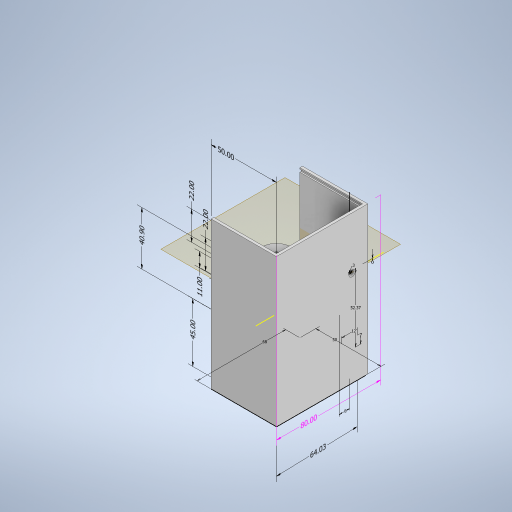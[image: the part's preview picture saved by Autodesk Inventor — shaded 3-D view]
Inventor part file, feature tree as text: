
AUTODESK INVENTOR PART (.ipt)
format: ipt  version: 2023 (Build 270158000, 158)  size: 996,352 bytes
history: native  units: in
note: dims shown in document units (in); Inventor stores cm internally (conversion verified against a paired STEP export)
features: extrude x23, sketch x22, other x10, fillet x2, plane x1
ambient origin geometry x8: Origin, YZ Plane, XZ Plane, XY Plane, X Axis, Y Axis, Z Axis, Center Point
bodies: Solid1 (feature_tree)
feature tree (58):
  other  "Annotations"
  sketch  "Sketch1"  dims[d0=2.6772in d1=1.9685in]
  extrude  "left wall"  Depth=1.9685in
  extrude  "bottom wall"  Depth=0.0787in
  extrude  "mid wall"  Depth=0.1181in
  extrude  "middle bearing hole"  Depth=1.8898in TaperAngle=0.0deg
  extrude  "back wall"  Depth=1.8898in TaperAngle=0.0deg
  extrude  "thicker mid wall ring for bearing"  Depth=4.3661in TaperAngle=0.0deg
  extrude  "motor attachment wall"  Depth=0.0197in TaperAngle=0.0deg
  extrude  "motor holes"  Depth=0.1142in
  extrude  "motor attachment wall cut out"  Depth=0.2323in
  extrude  "mid wall cut out"  Depth=1.8898in TaperAngle=0.0deg
  extrude  "encoder wall"  Depth=1.8898in
  extrude  "encoder holes"  Depth=0.9449in
  extrude  "encoder wall cut out"  Depth=0.1772in
  extrude  "top"  Depth=0.7087in
  sketch  "Sketch31"  dims[d136=0.9449in d137=0.9449in]
  extrude  "top rightWallGroove"  Depth=0.9449in
  extrude  "back rightWallGroove"  Depth=0.9449in
  extrude  "bottom rightWallGroove"  Depth=0.315in TaperAngle=0.0deg
  extrude  "encoder bearing thicker"  Depth=0.0787in
  plane  "Work Plane4"
  sketch  "Sketch38"  dims[d146=1.8898in d147=0.0in]
  extrude  "loadcell block"  TaperAngle=0.0deg  [1 undecoded]
  extrude  "wire exit"  Depth=0.2362in
  extrude  "loadcell screw holes"  Depth=0.1102in
  extrude  "Extrusion32"  Depth=1.8898in
  fillet  "Fillet1"  [1 undecoded]
  fillet  "Fillet2"  Radius=0.8661in
  extrude  "load cell block support"  Depth=1.8898in
  sketch  "Sketch3"  dims[d2=0.0787in d3=0.0in d4=0.0787in]
  sketch  "Sketch10"  dims[d5=4.3661in d6=0.0in d33=0.1181in]
  sketch  "Sketch11"  dims[d34=2.3189in d35=1.8898in d36=0.0in]
  sketch  "Sketch15"  dims[d37=0.2283in d38=1.8898in d39=0.0in]
  sketch  "Sketch20"  dims[d69=0.0787in d70=4.3661in d71=0.0in]
  sketch  "Sketch21"  dims[d106=0.315in d107=0.0197in d108=0.0in]
  sketch  "Sketch24"  dims[d110=1.7717in d111=0.1142in]
  sketch  "Sketch25"  dims[d112=3.1496in d113=0.0in d119=0.2323in]
  sketch  "Sketch27"  dims[d125=1.8898in d126=2.4606in]
  sketch  "Sketch29"  dims[d131=0.063in d132=0.1772in]
  sketch  "Sketch30"  dims[d133=0.1772in d134=0.7087in]
  sketch  "Sketch32"  dims[d138=0.9449in d139=0.9449in]
  sketch  "Sketch34"  dims[d140=0.315in d141=0.1772in d142=0.1211in d143=0.0in]
  sketch  "Sketch35"  dims[d144=3.3031in d145=0.0787in]
  sketch  "Sketch39"  dims[d153=0.2362in d154=0.3346in]
  sketch  "Sketch40"  dims[d155=0.3346in d156=0.1102in]
  sketch  "Sketch41"  dims[d157=0.1102in d158=1.8898in d159=0.0in d160=0.8661in d161=1.8898in d162=0.0in d163=0.0787in d164=0.0in d165=0.0394in d166=0.0787in d167=0.0394in d168=0.0in d169=0.0787in d170=0.0394in d171=0.0in d172=0.0394in d173=0.0787in d174=0.0394in d175=0.0394in d176=0.0in d177=0.0394in d178=0.0394in d179=0.0787in d180=0.0394in d181=0.0in d182=0.3543in d195=0.315in d196=0.0in d197=0.2756in d198=0.4724in d199=2.0618in d200=1.1811in d201=0.0in d202=0.1181in d203=1.1811in d204=0.0in d205=0.1378in d206=0.2362in d207=0.2362in d208=0.1181in d209=0.1181in d210=0.3937in d211=0.0in d215=0.5512in d216=0.0787in d217=0.0787in d218=0.3937in d219=0.0in d220=0.0787in d221=0.0394in d225=0.2756in d226=0.3937in d227=0.0in d185=0.3702in d186=0.133in d187=1.7717in d188=0.4331in d189=0.1142in d190=0.2139in d191=0.1379in d192=0.8661in d193=0.3032in d194=0.8661in d212=0.1205in d213=0.2186in d214=2.5209in d222=0.1531in d223=0.0332in d224=1.6102in d72=1.9685in d73=3.1496in d29=0.0197in d30=0.0344in d31=0.0197in d32=0.0344in d122=0.0197in]
  sketch  "Sketch26"  dims[d120=1.8898in d121=0.0in d123=0.1211in d124=0.0in]
  sketch  "Sketch28"  dims[d127=0.9449in d128=0.9449in]
  other  "Linear Dimension 2"
  other  "Linear Dimension 3"
  other  "Linear Dimension 4"
  other  "Linear Dimension 5"
  other  "Linear Dimension 6"
  other  "Linear Dimension 7"
  other  "Linear Dimension 8"
  other  "Linear Dimension 9"
  other  "Linear Dimension 10"
note: 2 required parameter values undecoded (feature->parameter linkage not recoverable at this tier; creation-order binding heuristic only, values carry confidence <= 0.55)
